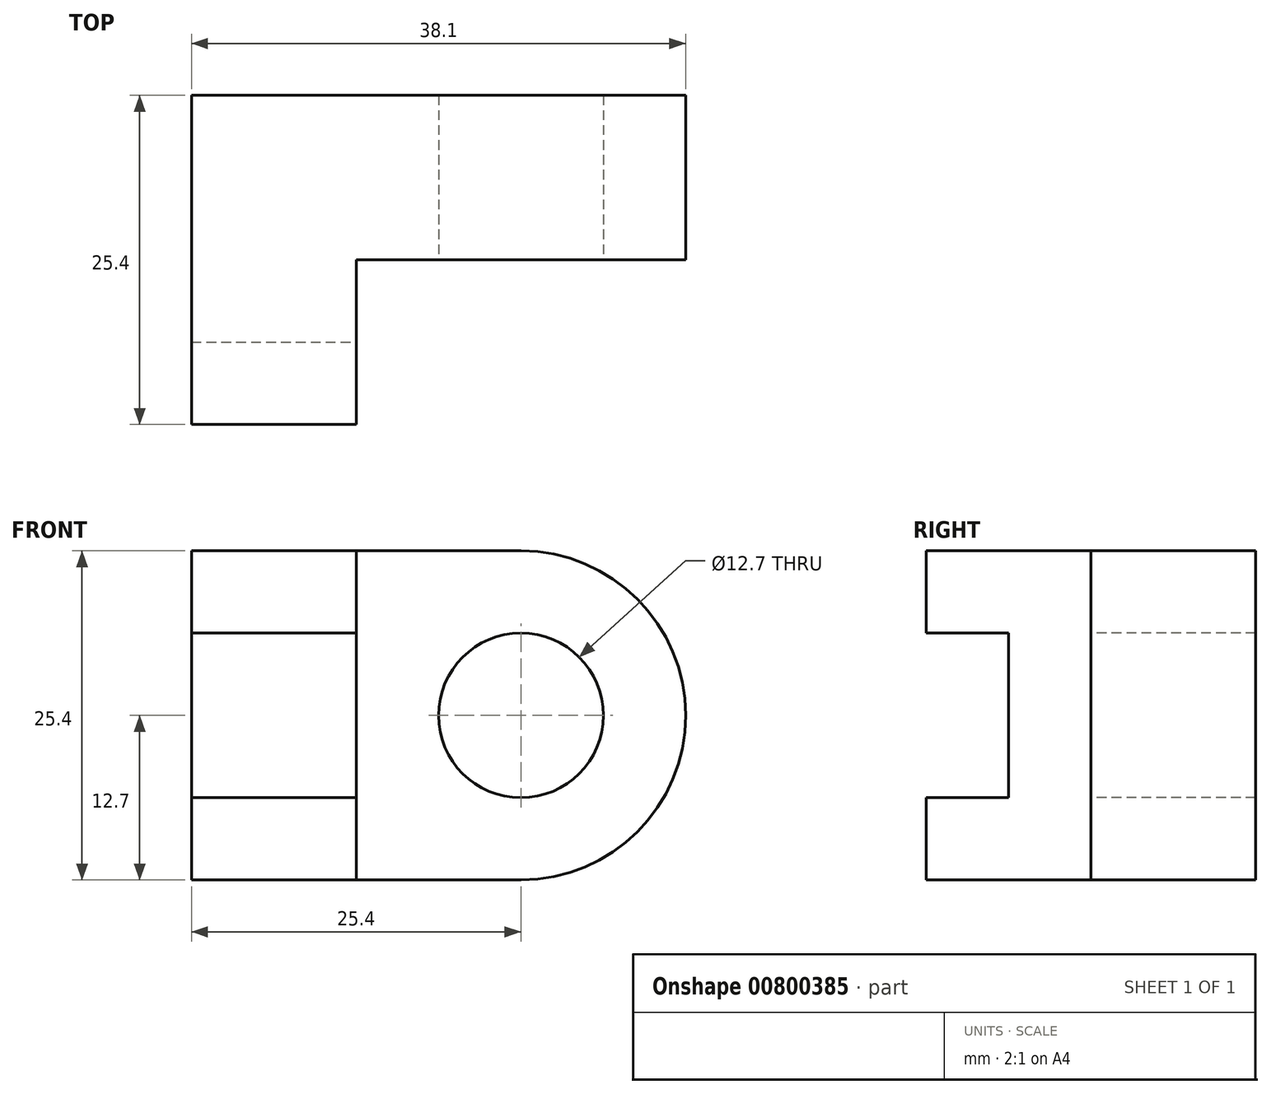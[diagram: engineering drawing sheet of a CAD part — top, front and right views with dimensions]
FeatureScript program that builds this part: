
annotation { "Feature Type Name" : "Feature", "Feature Type Description" : "" }
export const myFeature = defineFeature(function(context is Context, id is Id, definition is map)
    precondition{}
    {
        {
            var Q0;
            Q0=qCreatedBy(makeId("Top.planeOp"),FACE);
            var sketch = newSketch(context, id + "F0", { "sketchPlane" : qUnion([Q0])});
            skLineSegment(sketch, "E0", {"start": v(0, 0) * mm, "end": v(0, 25.4) * mm});
            skLineSegment(sketch, "E1", {"start": v(0, 25.4) * mm, "end": v(50.8, 25.4) * mm});
            skLineSegment(sketch, "E2", {"start": v(50.8, 25.4) * mm, "end": v(50.8, 12.7) * mm});
            skLineSegment(sketch, "E3", {"start": v(50.8, 12.7) * mm, "end": v(12.7, 12.7) * mm});
            skLineSegment(sketch, "E4", {"start": v(12.7, 12.7) * mm, "end": v(12.7, 0) * mm});
            skLineSegment(sketch, "E5", {"start": v(12.7, 0) * mm, "end": v(0, 0) * mm});
            skSolve(sketch);
        }
        {
            var Q0;
            Q0=makeQuery(id+"F0.imprint","IMPRINT",FACE,{"disambiguationData":[TD([[makeQuery(id+"F0.imprint","IMPRINT",EDGE,{"derivedFrom":sQuery(id+"F0.wireOp",EDGE,"E0")}),-1.0]])]});
            extrude(context, id + "F1", {"entities" : qUnion([Q0]), "depth" : 25.4 * mm, "offsetDistance" : 25.4 * mm});
        }
        {
            var Q0;
            Q0=makeQuery(id+"F1.opExtrude","SWEPT_FACE",FACE,{"disambiguationData":[OSD([sQuery(id+"F0.wireOp",EDGE,"E4")])]});
            var sketch = newSketch(context, id + "F2", { "sketchPlane" : qUnion([Q0])});
            skLineSegment(sketch, "E6", {"start": v(0, 25.4) * mm, "end": v(0, 19.05) * mm});
            skLineSegment(sketch, "E7", {"start": v(0, 19.05) * mm, "end": v(6.35, 19.05) * mm});
            skLineSegment(sketch, "E8", {"start": v(6.35, 19.05) * mm, "end": v(6.35, 6.35) * mm});
            skLineSegment(sketch, "E9", {"start": v(6.35, 6.35) * mm, "end": v(0, 6.35) * mm});
            skLineSegment(sketch, "E10", {"start": v(0, 6.35) * mm, "end": v(0, 0) * mm});
            skSolve(sketch);
        }
        {
            var Q0;
            {var subQ0=sQuery(id+"F2.wireOp",EDGE,"E7");Q0=makeQuery(id+"F2.imprint","IMPRINT",FACE,{"disambiguationData":[TD([[makeQuery(id+"F2.imprint","IMPRINT",EDGE,{"derivedFrom":subQ0}),-1.0]])]});}
            extrude(context, id + "F3", {"entities" : qUnion([Q0]), "operationType" : NewBodyOperationType.REMOVE, "oppositeDirection" : true, "depth" : 25.4 * mm, "offsetDistance" : 25.4 * mm});
        }
        {
            var Q0;
            Q0=makeQuery(id+"F1.opExtrude","SWEPT_FACE",FACE,{"disambiguationData":[OSD([sQuery(id+"F0.wireOp",EDGE,"E3")])]});
            var sketch = newSketch(context, id + "F4", { "sketchPlane" : qUnion([Q0])});
            skLineSegment(sketch, "E11", {"start": v(12.7, 25.4) * mm, "end": v(25.4, 25.4) * mm});
            skLineSegment(sketch, "E12", {"start": v(12.7, 0) * mm, "end": v(25.4, 0) * mm});
            skLineSegment(sketch, "E13", {"start": v(12.7, 12.7) * mm, "end": v(38.1, 12.7) * mm, "construction": true});
            skPoint(sketch, "E13.endSnap0", {"position": v(12.7, 12.7) * mm});
            skArc(sketch, "E14", {"start": v(25.4, 0) * mm, "mid": v(38.1, 12.7) * mm, "end": v(25.4, 25.4) * mm});
            skSolve(sketch);
        }
        {
            var Q0;
            {var subQ0=sQuery(id+"F4.wireOp",EDGE,"E14");Q0=makeQuery(id+"F4.imprint","IMPRINT",FACE,{"disambiguationData":[TD([[makeQuery(id+"F4.imprint","IMPRINT",EDGE,{"derivedFrom":subQ0}),-1.0]])]});}
            extrude(context, id + "F5", {"entities" : qUnion([Q0]), "operationType" : NewBodyOperationType.REMOVE, "oppositeDirection" : true, "depth" : 25.4 * mm, "offsetDistance" : 25.4 * mm});
        }
        {
            var Q0;
            Q0=makeQuery(id+"F1.opExtrude","SWEPT_FACE",FACE,{"disambiguationData":[OSD([sQuery(id+"F0.wireOp",EDGE,"E3")])]});
            var sketch = newSketch(context, id + "F6", { "sketchPlane" : qUnion([Q0])});
            skLineSegment(sketch, "E15", {"start": v(12.7, 12.7) * mm, "end": v(25.4, 12.7) * mm, "construction": true});
            skCircle(sketch, "E16", {"center": v(25.4, 12.7) * mm, "radius": 6.35 * mm});
            skSolve(sketch);
        }
        {
            var Q0;
            Q0=makeQuery(id+"F6.imprint","IMPRINT",FACE,{"disambiguationData":[TD([[makeQuery(id+"F6.imprint","IMPRINT",EDGE,{"derivedFrom":sQuery(id+"F6.wireOp",EDGE,"E16")}),1.0]])]});
            extrude(context, id + "F7", {"entities" : qUnion([Q0]), "operationType" : NewBodyOperationType.REMOVE, "oppositeDirection" : true, "depth" : 25.4 * mm, "offsetDistance" : 25.4 * mm});
        }
    });
